# Revit family: 305_639aa6f828fe485ca2be29ccbe0735
name_source: partatom
category: Pipe Accessories
revit_build: Autodesk Revit 2018 (Build: 20170223_1515(x64)
units: mm (PartAtom-declared; Revit-internal decimal feet)

## family parameters
Always vertical = Yes
Cut with Voids When Loaded = No
Part Type = Valve - Breaks Into
Round Connector Dimension = Use Diameter
Shared = No
Work Plane-Based = No

## types (11) — shared parameters
Description = Full port brass ball valve PN40/PN25
L2D = 39 mm
L2D_Min = 3048 mm
Manufacturer = VIR
QmdConnectorList = 301;D;302;D
URL = http://www.vironline.com
W2D = 10 mm  [stored 0.0328084 ft]
magiPartTypeId = 305
magiProductFamilyId = 639aa6f828fe485ca2be29ccbe0735

## per-type parameters (varying)
| type | CenSd_R1_6 | D | H11 | H12 | H12_2 | HL | L1 | L11 | L12 | L13 | L14 | L1__ve | L2 | L2__ve | L4 | L_2 | R1 | R11 | R2 | R3 | R4 | W12 | magiProductId |
| 340 DN10 | 8 mm  [stored 0.0262467 ft] | 10 mm | 23 mm | 3 mm  [stored 0.00984252 ft] | 1 mm  [stored 0.00328084 ft] | 41 mm | 9 mm  [stored 0.0295276 ft] | 6 mm | 14 mm  [stored 0.0459318 ft] | 19 mm  [stored 0.062336 ft] | 49 mm | -9 mm  [stored -0.0295276 ft] | 5 mm  [stored 0.0164042 ft] | -5 mm  [stored -0.0164042 ft] | 5 mm  [stored 0.0164042 ft] | 20 mm  [stored 0.0656168 ft] | 9 mm  [stored 0.0295276 ft] | 5 mm  [stored 0.0164042 ft] | 8 mm  [stored 0.0262467 ft] | 11 mm | 12 mm  [stored 0.0393701 ft] | 11 mm | dfd2c3bc6b1d47818ca9c6fe6e1204 |
| 340 DN100 | 62 mm | 100 mm | 99 mm | 7 mm | 3 mm  [stored 0.00984252 ft] | 144 mm | 31 mm | 17 mm  [stored 0.0557743 ft] | 48 mm | 65 mm | 169 mm | -31 mm  [stored -0.101706 ft] | 32 mm | -32 mm  [stored -0.104987 ft] | 32 mm | 94 mm | 72 mm | 13 mm  [stored 0.0426509 ft] | 57 mm | 69 mm | 79 mm | 33 mm | 6cf8eaaf76684abdb9abb9e6256cfa |
| 340 DN15 | 11 mm | 15 mm | 29 mm | 4 mm  [stored 0.0131234 ft] | 2 mm  [stored 0.00656168 ft] | 53 mm | 12 mm  [stored 0.0393701 ft] | 6 mm | 16 mm  [stored 0.0524934 ft] | 21 mm | 55 mm | -12 mm  [stored -0.0393701 ft] | 6 mm | -6 mm | 6 mm | 25 mm  [stored 0.082021 ft] | 13 mm  [stored 0.0426509 ft] | 5 mm  [stored 0.0164042 ft] | 10 mm  [stored 0.0328084 ft] | 14 mm  [stored 0.0459318 ft] | 15 mm  [stored 0.0492126 ft] | 13 mm  [stored 0.0426509 ft] | eae0144d20c24bfbb94863e952ffe7 |
| 340 DN20 | 14 mm  [stored 0.0459318 ft] | 20 mm | 33 mm | 4 mm  [stored 0.0131234 ft] | 2 mm  [stored 0.00656168 ft] | 57 mm | 12 mm  [stored 0.0393701 ft] | 7 mm | 16 mm  [stored 0.0524934 ft] | 21 mm | 55 mm | -12 mm  [stored -0.0393701 ft] | 9 mm  [stored 0.0295276 ft] | -9 mm  [stored -0.0295276 ft] | 9 mm  [stored 0.0295276 ft] | 29 mm | 16 mm  [stored 0.0524934 ft] | 6 mm | 13 mm  [stored 0.0426509 ft] | 17 mm  [stored 0.0557743 ft] | 19 mm  [stored 0.062336 ft] | 14 mm  [stored 0.0459318 ft] | 3bb0c95c44bc4bdfb465f4c26b0d20 |
| 340 DN25 | 17 mm  [stored 0.0557743 ft] | 25 mm | 38 mm | 4 mm  [stored 0.0131234 ft] | 2 mm  [stored 0.00656168 ft] | 65 mm | 15 mm  [stored 0.0492126 ft] | 8 mm  [stored 0.0262467 ft] | 22 mm | 29 mm | 76 mm | -15 mm  [stored -0.0492126 ft] | 9 mm  [stored 0.0295276 ft] | -9 mm  [stored -0.0295276 ft] | 9 mm  [stored 0.0295276 ft] | 34 mm | 20 mm  [stored 0.0656168 ft] | 6 mm | 16 mm  [stored 0.0524934 ft] | 20 mm  [stored 0.0656168 ft] | 23 mm | 15 mm  [stored 0.0492126 ft] | 0bf60d1fc7f04466ac0b14fc6a12f7 |
| 340 DN32 | 21 mm | 32 mm | 43 mm | 4 mm  [stored 0.0131234 ft] | 2 mm  [stored 0.00656168 ft] | 71 mm | 16 mm  [stored 0.0524934 ft] | 8 mm  [stored 0.0262467 ft] | 22 mm | 29 mm | 76 mm | -16 mm  [stored -0.0524934 ft] | 12 mm  [stored 0.0393701 ft] | -12 mm  [stored -0.0393701 ft] | 12 mm  [stored 0.0393701 ft] | 41 mm | 24 mm  [stored 0.0787402 ft] | 7 mm | 20 mm  [stored 0.0656168 ft] | 25 mm  [stored 0.082021 ft] | 28 mm | 17 mm  [stored 0.0557743 ft] | e27945260b974c61b39fca003efe9c |
| 340 DN40 | 26 mm | 40 mm | 50 mm | 4 mm  [stored 0.0131234 ft] | 2 mm  [stored 0.00656168 ft] | 79 mm | 17 mm  [stored 0.0557743 ft] | 9 mm  [stored 0.0295276 ft] | 24 mm  [stored 0.0787402 ft] | 33 mm | 85 mm | -17 mm  [stored -0.0557743 ft] | 15 mm  [stored 0.0492126 ft] | -15 mm  [stored -0.0492126 ft] | 15 mm  [stored 0.0492126 ft] | 47 mm | 30 mm | 8 mm  [stored 0.0262467 ft] | 24 mm  [stored 0.0787402 ft] | 30 mm | 34 mm | 19 mm  [stored 0.062336 ft] | 5f5da41725d84e7baf391dce99a28b |
| 340 DN50 | 32 mm | 50 mm | 57 mm | 5 mm  [stored 0.0164042 ft] | 2 mm  [stored 0.00656168 ft] | 87 mm | 19 mm  [stored 0.062336 ft] | 11 mm | 24 mm  [stored 0.0787402 ft] | 33 mm | 85 mm | -19 mm  [stored -0.062336 ft] | 18 mm  [stored 0.0590551 ft] | -18 mm  [stored -0.0590551 ft] | 18 mm  [stored 0.0590551 ft] | 55 mm | 37 mm | 8 mm  [stored 0.0262467 ft] | 30 mm | 37 mm | 42 mm | 21 mm | 318cdcff8f5f46dc887244166be6ad |
| 340 DN65 | 41 mm | 65 mm | 75 mm | 6 mm | 3 mm  [stored 0.00984252 ft] | 117 mm | 25 mm  [stored 0.082021 ft] | 12 mm  [stored 0.0393701 ft] | 34 mm | 46 mm | 121 mm | -25 mm  [stored -0.082021 ft] | 23 mm | -23 mm  [stored -0.0754593 ft] | 23 mm | 71 mm | 48 mm | 10 mm  [stored 0.0328084 ft] | 38 mm | 46 mm | 53 mm | 25 mm  [stored 0.082021 ft] | 5d550d003e184e659b91a3e350acca |
| 340 DN8 | 7 mm | 8 mm | 22 mm | 3 mm  [stored 0.00984252 ft] | 1 mm  [stored 0.00328084 ft] | 41 mm | 9 mm  [stored 0.0295276 ft] | 5 mm  [stored 0.0164042 ft] | 14 mm  [stored 0.0459318 ft] | 19 mm  [stored 0.062336 ft] | 49 mm | -9 mm  [stored -0.0295276 ft] | 5 mm  [stored 0.0164042 ft] | -5 mm  [stored -0.0164042 ft] | 5 mm  [stored 0.0164042 ft] | 20 mm  [stored 0.0656168 ft] | 8 mm  [stored 0.0262467 ft] | 4 mm  [stored 0.0131234 ft] | 6 mm | 9 mm  [stored 0.0295276 ft] | 10 mm  [stored 0.0328084 ft] | 11 mm | 21158be5a0a2446d8b4cf4c6577bb9 |
| 340 DN80 | 50 mm | 80 mm | 86 mm | 7 mm | 3 mm  [stored 0.00984252 ft] | 132 mm | 27 mm | 14 mm  [stored 0.0459318 ft] | 48 mm | 65 mm | 169 mm | -27 mm  [stored -0.0885827 ft] | 27 mm | -27 mm  [stored -0.0885827 ft] | 27 mm | 82 mm | 58 mm | 11 mm | 46 mm | 56 mm | 64 mm | 29 mm | 9a11034f74f3416f9403c95fee8a7a |

note: column(s) folded — value = type name in every type: MC Product Code

note: [stored X ft] marks values corroborated as IEEE doubles in the binary element streams (Revit-internal decimal feet)

## geometry (parser evidence)
native form markers: Sweep x1
no freeform markers — native parametric forms only
